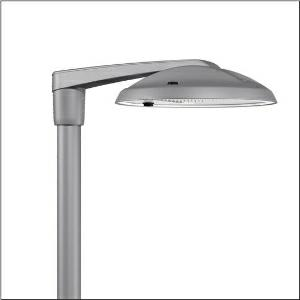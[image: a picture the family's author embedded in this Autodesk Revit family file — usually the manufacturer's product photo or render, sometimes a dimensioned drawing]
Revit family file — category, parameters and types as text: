
# Revit family: dl_50_iq_mini___st1_0a_5xa248d31y08me_2069
name_source: partatom
category: Lighting Fixtures
units: mm (PartAtom-declared; Revit-internal decimal feet)

## family parameters
Cut with Voids When Loaded = No
Host = Face
Light Source = No
Part Type = Normal
Room Calculation Point = No
Round Connector Dimension = Use Diameter
Shared = No

## types (1)
- --- (1 x LED, 15720 lm, 107 W, 3000K)
    Apparent Load = 107 VA
    CIE Flux Codes = 37 72 97 100 100
    Color Rendering = 70
    Color Temperature = 3000K
    Default Elevation = 1800 mm
    Description = DL 50 iQ mini, mast luminaire, primary light control with lens, of PMMA, primary optical cover: cover, of toughened safety glass, transparent, light distribution: ST1.0a, light emission: direct distribution, primary light characteristic: asymmetric, installation type: post-top, side-entry, LED, High Power LED, rated luminous flux: 15.720lm, luminous efficacy: 147lm/W, light colour: 730, colour temperature: 3000K, control gear: iQ-Street Remote, D4i with power reduction, control: optimised constant luminous flux control (CLO 2.0), Desk-Remote (wireless, voltage-free reading and setting of iQ features in the workshop via application-optimized NFC function/RFID function), Light-Fading, Smart-Wire, Night-Set, Lumen-Switch, Temp-Guard, Auto-Match, Street-Remote, pre-setting: logarithmic dimming characteristic, mains connection: 230..240V, AC, 50/60Hz, connection cable pre-assembled, cable length: 10,5m, start of lifetime: 107W, end of service life: 113W, reduction: 47W, luminaire housing, of diecast aluminium, powder-coated, SITECO metallic grey (DB 702S), inclination adjustable: 0°, 5°, 10° (post-top) | 0°, -5°, -10°, -15° (side-entry), please order mast post-top element or mast side-entry element separately, diameter: 500mm, height: 115mm, post-top: for spigot size d x l = 76 x 100mm; with reducer (optional accessory) 60 x 100mm | side-entry: for spigot size d x l = 60 x 100mm; with reducer (optional accessory) 42 x 100mm, mounting height: 4..6m, Smart Interface below and above, protection rating (complete): IP66, insulation class (complete): insulation class II (safety insulation), certification: CE, ENEC, ENEC+, VDE, impact resistance: IK08, permissible operating ambient temperature for outdoor applications: -25..+40°C, standard-compliant lighting for roads and squares, packaging unit: 1 piece

Light Distribution: ST1.0a
    Height = 115 mm
    Lamp = 1 x LED
    Lamp Light Flux = 15720 lm
    Lamp Power = 107 W
    Lamp count = 1
    Length = 500 mm
    Luminous efficacy = 147 lm/W
    Manufacturer = Siteco
    ModVariant = No
    Model = 5XA248D31Y08ME
    Number of Poles = 1
    OnlyDefault = Yes
    Power Factor = 1
    Product Name = DL 50 iQ mini | ST1.0a
    Product group = mast luminaire | pylon top
    ProductGroupID = 6100
    Protection Class = Protection class II
    Protection Degree = IP 66
    RLX_Detail_Level = 1
    RLX_Emergency_Light_Flux = 0 lm
    RLX_Emergency_Type = 0
    RLX_Emergency_Type_DB = No
    RlxData = <blob elided: 106965 chars, md5=8c3fcc41>
    Socket = socket
    Standby Power = 0 W
    System Light Flux = 15720 lm
    System Power = 107 W
    Type Comments = factory setting: luminous flux: 100 % | dim-lin: 254 | 565 mA
    Type Image = l_1251786.jpg
    URL = http://relux.com
    VarID = @adj_073053
    Voltage = 0 V
    Weight = 0.00 kg
    Width = 0 mm  [stored 0 ft]

note: [stored X ft] marks values corroborated as IEEE doubles in the binary element streams (Revit-internal decimal feet)

## geometry (parser evidence)
native form markers: Blend x4, Sweep x10
no freeform markers — native parametric forms only
